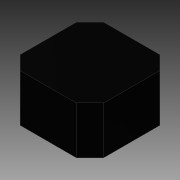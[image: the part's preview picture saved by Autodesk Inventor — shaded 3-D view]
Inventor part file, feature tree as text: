
AUTODESK INVENTOR PART (.ipt)
format: ipt  version: 2016 (Build 200138000, 138)  size: 75,776 bytes
history: native  units: mm
features: reference x8, extrude x1, sketch x1
ambient origin geometry x8: Origin, YZ Plane, XZ Plane, XY Plane, X Axis, Y Axis, Z Axis, Center Point
bodies: Solid1 (feature_tree)
feature tree (10):
  extrude  "Extrusion1"  [1 undecoded]
  sketch  "Sketch1"  dims[d0=24.0mm d1=0.0mm]
  reference  "Reference1"
  reference  "Reference2"
  reference  "Reference3"
  reference  "Reference4"
  reference  "Reference5"
  reference  "Reference6"
  reference  "Reference7"
  reference  "Reference8"
note: 1 required parameter value undecoded (feature->parameter linkage not recoverable at this tier; creation-order binding heuristic only, values carry confidence <= 0.55)
